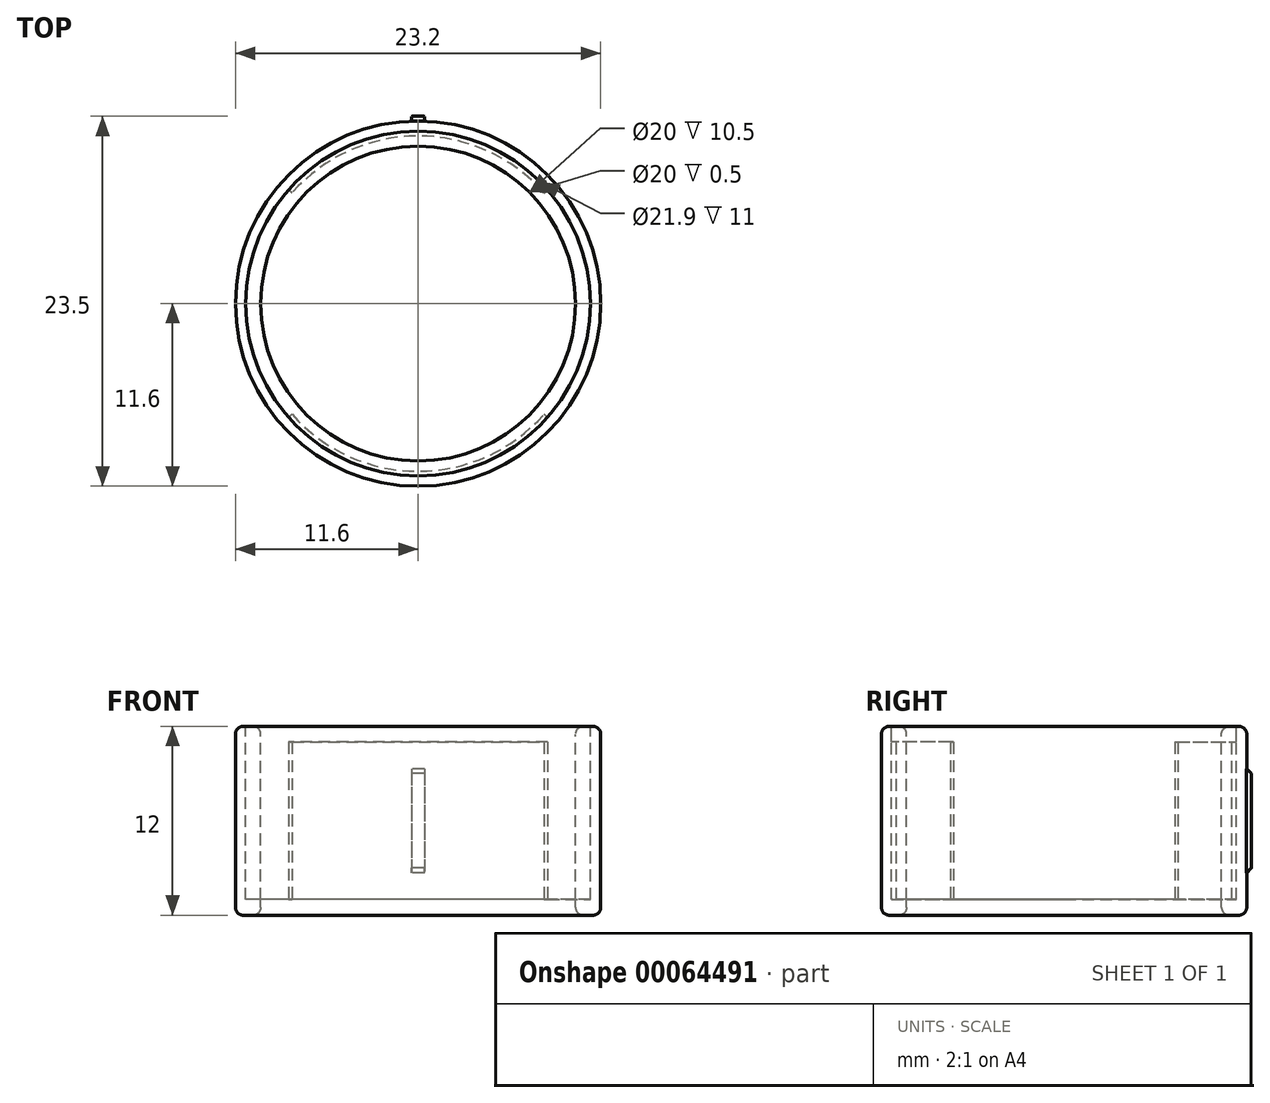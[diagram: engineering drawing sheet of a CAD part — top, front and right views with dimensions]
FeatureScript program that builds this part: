
annotation { "Feature Type Name" : "Feature", "Feature Type Description" : "" }
export const myFeature = defineFeature(function(context is Context, id is Id, definition is map)
    precondition{}
    {
        {
            assignVariable(context, id + "F0", {"name" : "innerDiameter", "anyValue" : 20});
        }
        {
            assignVariable(context, id + "F1", {"name" : "circuitLength", "anyValue" : 17});
        }
        {
            var Q0;
            Q0=qCreatedBy(makeId("Right.planeOp"),FACE);
            var sketch = newSketch(context, id + "F2", { "sketchPlane" : qUnion([Q0])});
            skLineSegment(sketch, "E0.bottom", {"start": v(10.65, 11) * mm, "end": v(10.95, 11) * mm});
            skLineSegment(sketch, "E0.top", {"start": v(10.65, 1) * mm, "end": v(10.95, 1) * mm});
            skLineSegment(sketch, "E0.left", {"start": v(10.95, 11) * mm, "end": v(10.95, 1) * mm});
            skLineSegment(sketch, "E0.right", {"start": v(10.65, 11) * mm, "end": v(10.65, 1) * mm});
            skLineSegment(sketch, "E1", {"start": v(10.8, 12) * mm, "end": v(10.8, 11) * mm, "construction": true});
            skLineSegment(sketch, "E2", {"start": v(10.8, 0) * mm, "end": v(10.8, 1) * mm, "construction": true});
            skLineSegment(sketch, "E3", {"start": v(0, 27.89) * mm, "end": v(0, 0) * mm, "construction": true});
            skLineSegment(sketch, "E4.bottom", {"start": v(-10.95, 11) * mm, "end": v(-10.65, 11) * mm});
            skLineSegment(sketch, "E4.top", {"start": v(-10.95, 1) * mm, "end": v(-10.65, 1) * mm});
            skLineSegment(sketch, "E4.left", {"start": v(-10.95, 11) * mm, "end": v(-10.95, 1) * mm});
            skLineSegment(sketch, "E4.right", {"start": v(-10.65, 11) * mm, "end": v(-10.65, 1) * mm});
            skLineSegment(sketch, "E5.bottom", {"start": v(10, 12) * mm, "end": v(11.6, 12) * mm});
            skLineSegment(sketch, "E5.top", {"start": v(10, 0) * mm, "end": v(11.6, 0) * mm});
            skLineSegment(sketch, "E5.left", {"start": v(10, 12) * mm, "end": v(10, 0) * mm});
            skLineSegment(sketch, "E5.right", {"start": v(11.6, 12) * mm, "end": v(11.6, 9.3) * mm});
            skLineSegment(sketch, "E6", {"start": v(10.95, 11) * mm, "end": v(10.95, 12) * mm});
            skLineSegment(sketch, "E7", {"start": v(10.65, 1) * mm, "end": v(10, 1) * mm});
            skLineSegment(sketch, "E8.bottom", {"start": v(11.6, 9.3) * mm, "end": v(11.9, 9) * mm});
            skLineSegment(sketch, "E8.top", {"start": v(11.6, 2.7) * mm, "end": v(11.9, 3) * mm});
            skLineSegment(sketch, "E8.right", {"start": v(11.9, 9) * mm, "end": v(11.9, 3) * mm});
            skLineSegment(sketch, "E9", {"start": v(11.6, 9.3) * mm, "end": v(11.6, 2.7) * mm});
            skLineSegment(sketch, "E10", {"start": v(11.6, 2.7) * mm, "end": v(11.6, 0) * mm});
            skSolve(sketch);
        }
        {
            var Q0;
            Q0=makeQuery(id+"F2.imprint","IMPRINT",FACE,{"disambiguationData":[TD([[makeQuery(id+"F2.imprint","IMPRINT",EDGE,{"derivedFrom":sQuery(id+"F2.wireOp",EDGE,"E0.top")}),-1.0]])]});
            var Q1;
            Q1=sQuery(id+"F2.wireOp",EDGE,"E3");
            revolve(context, id + "F3", {"entities" : qUnion([Q0]), "axis" : qUnion([Q1]), "revolveType" : RevolveType.FULL});
        }
        {
            var Q0;
            Q0=makeQuery(id+"F2.imprint","IMPRINT",FACE,{"disambiguationData":[TD([[makeQuery(id+"F2.imprint","IMPRINT",EDGE,{"derivedFrom":sQuery(id+"F2.wireOp",EDGE,"E0.bottom")}),1.0]])]});
            var Q1;
            Q1=makeQuery(id+"F2.imprint","IMPRINT",FACE,{"disambiguationData":[TD([[makeQuery(id+"F2.imprint","IMPRINT",EDGE,{"derivedFrom":sQuery(id+"F2.wireOp",EDGE,"E0.bottom")}),-1.0]])]});
            var Q2;
            Q2=sQuery(id+"F2.wireOp",EDGE,"E3");
            revolve(context, id + "F4", {"entities" : qUnion([Q0, Q1]), "axis" : qUnion([Q2]), "revolveType" : RevolveType.FULL});
        }
        {
            var Q0;
            Q0=makeQuery(id+"F2.imprint","IMPRINT",FACE,{"disambiguationData":[TD([[makeQuery(id+"F2.imprint","IMPRINT",EDGE,{"derivedFrom":sQuery(id+"F2.wireOp",EDGE,"E0.bottom")}),-1.0]])]});
            var Q1;
            Q1=makeQuery(id+"F2.imprint","IMPRINT",FACE,{"disambiguationData":[TD([[makeQuery(id+"F2.imprint","IMPRINT",EDGE,{"derivedFrom":sQuery(id+"F2.wireOp",EDGE,"E4.bottom")}),-1.0]])]});
            var Q2;
            Q2=sQuery(id+"F2.wireOp",EDGE,"E3");
            revolve(context, id + "F5", {"operationType" : NewBodyOperationType.REMOVE, "entities" : qUnion([Q0, Q1]), "axis" : qUnion([Q2]), "revolveType" : RevolveType.SYMMETRIC, "angle" : 2 * (180 / 3.14) * (getVariable(context, 'circuitLength') / getVariable(context, 'innerDiameter')) * degree});
        }
        {
            var Q0;
            Q0=makeQuery(id+"F2.imprint","IMPRINT",FACE,{"disambiguationData":[TD([[makeQuery(id+"F2.imprint","IMPRINT",EDGE,{"derivedFrom":sQuery(id+"F2.wireOp",EDGE,"E8.bottom")}),-1.0]])]});
            var Q1;
            Q1=sQuery(id+"F2.wireOp",EDGE,"E3");
            revolve(context, id + "F6", {"operationType" : NewBodyOperationType.ADD, "entities" : qUnion([Q0]), "axis" : qUnion([Q1]), "revolveType" : RevolveType.SYMMETRIC, "angle" : 4 * degree});
        }
        {
            var Q0;
            Q0=makeQuery(id+"F4.opRevolve","SWEPT_EDGE",EDGE,{"disambiguationData":[OSD([sQuery(id+"F2.wireOp",EDGE,"E5.bottom"),sQuery(id+"F2.wireOp",EDGE,"E5.left")])]});
            var Q1;
            Q1=makeQuery(id+"F3.opRevolve","SWEPT_EDGE",EDGE,{"disambiguationData":[OSD([sQuery(id+"F2.wireOp",EDGE,"E5.bottom"),sQuery(id+"F2.wireOp",EDGE,"E5.right")])]});
            var Q2;
            Q2=makeQuery(id+"F3.opRevolve","SWEPT_EDGE",EDGE,{"disambiguationData":[OSD([sQuery(id+"F2.wireOp",EDGE,"E5.top"),sQuery(id+"F2.wireOp",EDGE,"E5.right")])]});
            var Q3;
            Q3=makeQuery(id+"F3.opRevolve","SWEPT_EDGE",EDGE,{"disambiguationData":[OSD([sQuery(id+"F2.wireOp",EDGE,"E5.top"),sQuery(id+"F2.wireOp",EDGE,"E5.left")])]});
            fillet(context, id + "F7", {"entities" : qUnion([Q0, Q1, Q2, Q3]), "radius" : 0.5 * mm, "tangentPropagation" : true, "allowEdgeOverflow" : false});
        }
    });
